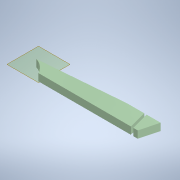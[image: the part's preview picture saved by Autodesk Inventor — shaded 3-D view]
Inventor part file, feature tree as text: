
AUTODESK INVENTOR PART (.ipt)
format: ipt  version: 2022 (Build 260153000, 153)  size: 112,640 bytes
history: native  units: mm
features: other x2, extrude x1, sketch x1
ambient origin geometry x8: Origin, YZ Plane, XZ Plane, XY Plane, X Axis, Y Axis, Z Axis, Center Point
bodies: Body1 (feature_tree)
feature tree (4):
  other  "Твердое тело1"
  other  "РабПлоскость1"
  extrude  "Выдавливание1"  Depth=5.0mm TaperAngle=0.0deg
  sketch  "Эскиз1"
